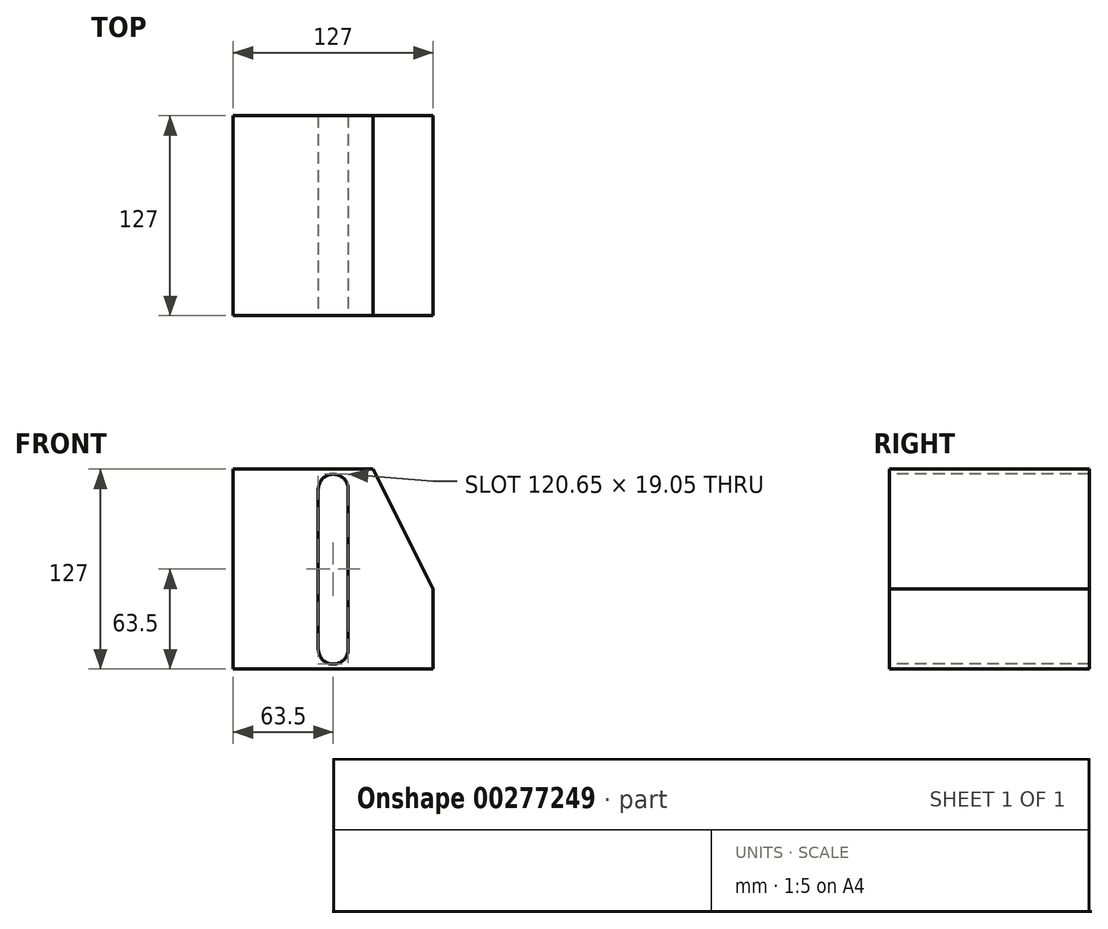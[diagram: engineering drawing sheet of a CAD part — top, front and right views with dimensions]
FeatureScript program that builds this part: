
annotation { "Feature Type Name" : "Feature", "Feature Type Description" : "" }
export const myFeature = defineFeature(function(context is Context, id is Id, definition is map)
    precondition{}
    {
        {
            var Q0;
            Q0=qCreatedBy(makeId("Front.planeOp"),FACE);
            var sketch = newSketch(context, id + "F0", { "sketchPlane" : qUnion([Q0])});
            skLineSegment(sketch, "E0.bottom", {"start": v(0, 0) * mm, "end": v(127, 0) * mm});
            skLineSegment(sketch, "E0.top", {"start": v(0, 127) * mm, "end": v(127, 127) * mm});
            skLineSegment(sketch, "E0.left", {"start": v(0, 0) * mm, "end": v(0, 127) * mm});
            skLineSegment(sketch, "E0.right", {"start": v(127, 0) * mm, "end": v(127, 127) * mm});
            skSolve(sketch);
        }
        {
            var Q0;
            Q0=makeQuery(id+"F0.imprint","IMPRINT",FACE,{"disambiguationData":[TD([[makeQuery(id+"F0.imprint","IMPRINT",EDGE,{"derivedFrom":sQuery(id+"F0.wireOp",EDGE,"E0.bottom")}),1.0]])]});
            extrude(context, id + "F1", {"entities" : qUnion([Q0]), "depth" : 127 * mm});
        }
        {
            var Q0;
            Q0=makeQuery(id+"F1.opExtrude","CAP_FACE",FACE,{"disambiguationData":[OSD([sQuery(id+"F0.wireOp",EDGE,"E0.bottom"),sQuery(id+"F0.wireOp",EDGE,"E0.top"),sQuery(id+"F0.wireOp",EDGE,"E0.left"),sQuery(id+"F0.wireOp",EDGE,"E0.right")])],"isStart":false});
            var sketch = newSketch(context, id + "F2", { "sketchPlane" : qUnion([Q0])});
            skArc(sketch, "E1", {"start": v(73.03, 114.3) * mm, "mid": v(63.5, 123.83) * mm, "end": v(53.98, 114.3) * mm});
            skArc(sketch, "E2", {"start": v(53.98, 12.7) * mm, "mid": v(63.5, 3.18) * mm, "end": v(73.03, 12.7) * mm});
            skLineSegment(sketch, "E3", {"start": v(53.98, 114.3) * mm, "end": v(53.98, 12.7) * mm});
            skLineSegment(sketch, "E4", {"start": v(73.02, 114.3) * mm, "end": v(73.02, 12.7) * mm});
            skSolve(sketch);
        }
        {
            var Q0;
            Q0 = qSketchRegion(id + "F2", true);
            var Q1;
            Q1=makeQuery(id+"F1.opExtrude","CAP_FACE",FACE,{"disambiguationData":[OSD([sQuery(id+"F0.wireOp",EDGE,"E0.bottom"),sQuery(id+"F0.wireOp",EDGE,"E0.top"),sQuery(id+"F0.wireOp",EDGE,"E0.left"),sQuery(id+"F0.wireOp",EDGE,"E0.right")])],"isStart":true});
            extrude(context, id + "F3", {"entities" : qUnion([Q0]), "operationType" : NewBodyOperationType.REMOVE, "endBound" : BoundingType.UP_TO_SURFACE, "oppositeDirection" : true, "endBoundEntityFace" : qUnion([Q1]), "depth" : 25.4 * mm});
        }
        {
            var Q0;
            Q0=makeQuery(id+"F1.opExtrude","SWEPT_EDGE",EDGE,{"disambiguationData":[OSD([sQuery(id+"F0.wireOp",EDGE,"E0.top"),sQuery(id+"F0.wireOp",EDGE,"E0.right")])]});
            chamfer(context, id + "F4", {"entities" : qUnion([Q0]), "chamferType" : ChamferType.TWO_OFFSETS, "width1" : 38.1 * mm, "oppositeDirection" : false, "width2" : 76.2 * mm, "tangentPropagation" : true});
        }
    });
